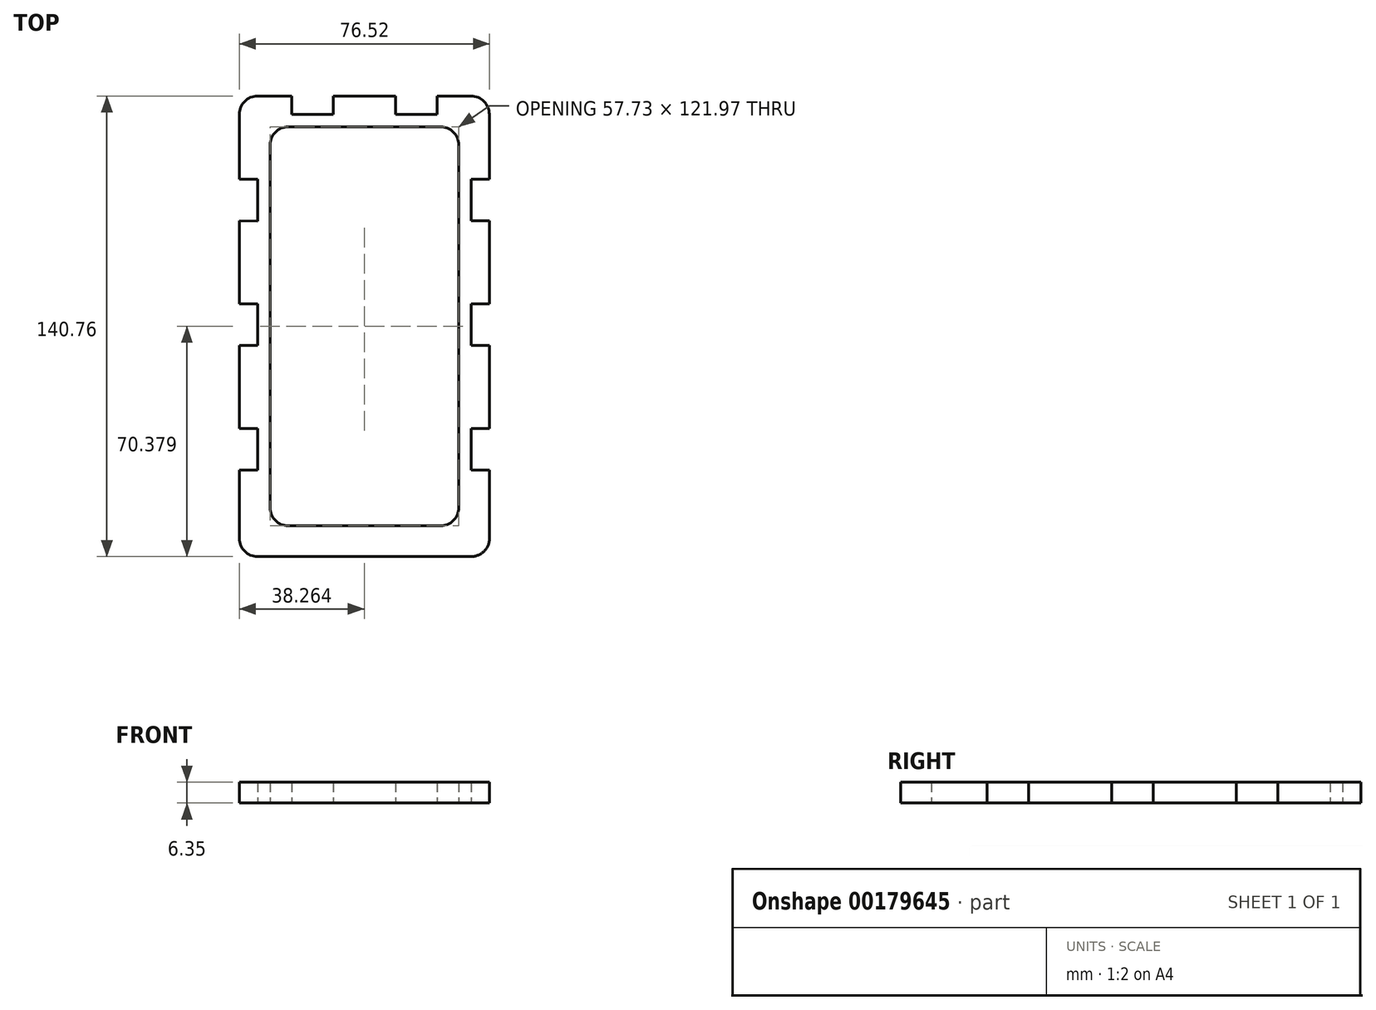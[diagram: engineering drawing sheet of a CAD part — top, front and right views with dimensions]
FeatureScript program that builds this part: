
annotation { "Feature Type Name" : "Feature", "Feature Type Description" : "" }
export const myFeature = defineFeature(function(context is Context, id is Id, definition is map)
    precondition{}
    {
        {
            var Q0;
            Q0=qCreatedBy(makeId("Top.planeOp"),FACE);
            var sketch = newSketch(context, id + "F0", { "sketchPlane" : qUnion([Q0])});
            skLineSegment(sketch, "E0.0", {"start": v(-32.64, 69.1) * mm, "end": v(-22.23, 69.1) * mm});
            skLineSegment(sketch, "E0.1", {"start": v(-38.23, 63.5) * mm, "end": v(-38.23, 43.7) * mm});
            skLineSegment(sketch, "E0.2", {"start": v(-32.64, -71.67) * mm, "end": v(-22.23, -71.67) * mm});
            skLineSegment(sketch, "E0.3", {"start": v(38.23, 63.5) * mm, "end": v(38.23, 43.7) * mm});
            skPoint(sketch, "E1", {"position": v(-38.23, 43.7) * mm});
            skPoint(sketch, "E2", {"position": v(38.23, 43.7) * mm});
            skPoint(sketch, "E3", {"position": v(-38.23, 31) * mm});
            skPoint(sketch, "E4", {"position": v(38.23, 31) * mm});
            skLineSegment(sketch, "E5", {"start": v(-38.23, 43.7) * mm, "end": v(-32.64, 43.7) * mm});
            skLineSegment(sketch, "E6", {"start": v(-38.23, 31) * mm, "end": v(-32.64, 30.78) * mm});
            skLineSegment(sketch, "E7", {"start": v(-32.64, 30.78) * mm, "end": v(-32.64, 43.7) * mm});
            skLineSegment(sketch, "E8.trimOffspring", {"start": v(-38.23, 31) * mm, "end": v(-38.23, 5.6) * mm});
            skLineSegment(sketch, "E9", {"start": v(38.23, 43.7) * mm, "end": v(32.64, 43.7) * mm});
            skLineSegment(sketch, "E10", {"start": v(38.23, 31) * mm, "end": v(32.64, 31) * mm});
            skLineSegment(sketch, "E11", {"start": v(32.64, 31) * mm, "end": v(32.64, 43.7) * mm});
            skLineSegment(sketch, "E12.trimOffspring", {"start": v(38.23, 31) * mm, "end": v(38.23, 5.6) * mm});
            skPoint(sketch, "E13", {"position": v(-38.23, 5.6) * mm});
            skPoint(sketch, "E14", {"position": v(38.23, 5.6) * mm});
            skPoint(sketch, "E15", {"position": v(-38.23, -7.1) * mm});
            skPoint(sketch, "E16", {"position": v(38.23, -7.1) * mm});
            skPoint(sketch, "E17", {"position": v(-38.23, -32.5) * mm});
            skPoint(sketch, "E18", {"position": v(38.23, -32.5) * mm});
            skPoint(sketch, "E19", {"position": v(38.23, -45.2) * mm});
            skLineSegment(sketch, "E20", {"start": v(-38.23, 5.6) * mm, "end": v(-32.64, 5.6) * mm});
            skLineSegment(sketch, "E21", {"start": v(-38.23, -7.1) * mm, "end": v(-32.64, -7.1) * mm});
            skLineSegment(sketch, "E22", {"start": v(-32.64, -7.1) * mm, "end": v(-32.64, 5.6) * mm});
            skLineSegment(sketch, "E23.trimOffspring", {"start": v(-38.23, -7.1) * mm, "end": v(-38.23, -32.5) * mm});
            skLineSegment(sketch, "E24.trimOffspring", {"start": v(-38.23, -52.57) * mm, "end": v(-38.23, -66.09) * mm});
            skLineSegment(sketch, "E25", {"start": v(-38.23, -32.5) * mm, "end": v(-32.64, -32.5) * mm});
            skLineSegment(sketch, "E26", {"start": v(-38.23, -45.2) * mm, "end": v(-32.64, -45.2) * mm});
            skLineSegment(sketch, "E27", {"start": v(-32.64, -45.2) * mm, "end": v(-32.64, -32.5) * mm});
            skLineSegment(sketch, "E28", {"start": v(38.23, 5.6) * mm, "end": v(32.64, 5.6) * mm});
            skLineSegment(sketch, "E29", {"start": v(38.23, -7.1) * mm, "end": v(32.64, -7.1) * mm});
            skLineSegment(sketch, "E30", {"start": v(32.64, -7.1) * mm, "end": v(32.64, 5.6) * mm});
            skLineSegment(sketch, "E31.trimOffspring", {"start": v(38.23, -7.1) * mm, "end": v(38.23, -32.5) * mm});
            skLineSegment(sketch, "E32", {"start": v(38.23, -32.5) * mm, "end": v(32.64, -32.5) * mm});
            skLineSegment(sketch, "E33", {"start": v(38.23, -45.2) * mm, "end": v(32.64, -45.2) * mm});
            skLineSegment(sketch, "E34", {"start": v(32.64, -45.2) * mm, "end": v(32.64, -32.5) * mm});
            skLineSegment(sketch, "E35.trimOffspring", {"start": v(38.23, -52.57) * mm, "end": v(38.3, -66.06) * mm});
            skLineSegment(sketch, "E36", {"start": v(-38.23, -45.2) * mm, "end": v(-38.23, -52.57) * mm});
            skLineSegment(sketch, "E37", {"start": v(38.23, -45.2) * mm, "end": v(38.23, -52.57) * mm});
            skPoint(sketch, "E38", {"position": v(-22.23, 69.1) * mm});
            skPoint(sketch, "E39", {"position": v(-9.53, 69.1) * mm});
            skPoint(sketch, "E40", {"position": v(9.52, 69.1) * mm});
            skPoint(sketch, "E41", {"position": v(22.22, 69.1) * mm});
            skLineSegment(sketch, "E42", {"start": v(-22.23, 69.1) * mm, "end": v(-22.23, 63.5) * mm});
            skLineSegment(sketch, "E43", {"start": v(-9.53, 69.1) * mm, "end": v(-9.53, 63.5) * mm});
            skLineSegment(sketch, "E44", {"start": v(-9.53, 63.5) * mm, "end": v(-22.23, 63.5) * mm});
            skLineSegment(sketch, "E45.trimOffspring", {"start": v(-9.53, 69.1) * mm, "end": v(9.52, 69.1) * mm});
            skLineSegment(sketch, "E46", {"start": v(9.52, 69.1) * mm, "end": v(9.52, 63.5) * mm});
            skLineSegment(sketch, "E47", {"start": v(22.22, 69.1) * mm, "end": v(22.22, 63.5) * mm});
            skLineSegment(sketch, "E48.trimOffspring", {"start": v(22.22, 69.1) * mm, "end": v(32.64, 69.1) * mm});
            skLineSegment(sketch, "E49", {"start": v(9.52, 63.5) * mm, "end": v(22.22, 63.5) * mm});
            skPoint(sketch, "E50", {"position": v(-22.23, -71.67) * mm});
            skPoint(sketch, "E51", {"position": v(-9.53, -71.67) * mm});
            skPoint(sketch, "E52", {"position": v(9.52, -71.67) * mm});
            skPoint(sketch, "E53", {"position": v(22.22, -71.67) * mm});
            skLineSegment(sketch, "E54.trimOffspring", {"start": v(-9.53, -71.67) * mm, "end": v(9.52, -71.67) * mm});
            skLineSegment(sketch, "E55.trimOffspring", {"start": v(22.22, -71.67) * mm, "end": v(32.7, -71.67) * mm});
            skPoint(sketch, "E56.visualSharp", {"position": v(-38.23, 69.1) * mm});
            skArc(sketch, "E56.filletArc", {"start": v(-32.64, 69.1) * mm, "mid": v(-36.6, 67.46) * mm, "end": v(-38.23, 63.5) * mm});
            skPoint(sketch, "E57.visualSharp", {"position": v(38.23, 69.1) * mm});
            skArc(sketch, "E57.filletArc", {"start": v(38.23, 63.5) * mm, "mid": v(36.6, 67.46) * mm, "end": v(32.64, 69.1) * mm});
            skPoint(sketch, "E58.visualSharp", {"position": v(38.32, -71.67) * mm});
            skArc(sketch, "E58.filletArc", {"start": v(32.7, -71.67) * mm, "mid": v(36.67, -70.03) * mm, "end": v(38.3, -66.06) * mm});
            skPoint(sketch, "E59.visualSharp", {"position": v(-38.23, -71.67) * mm});
            skArc(sketch, "E59.filletArc", {"start": v(-38.23, -66.09) * mm, "mid": v(-36.6, -70.04) * mm, "end": v(-32.64, -71.67) * mm});
            skLineSegment(sketch, "E60", {"start": v(-32.64, -71.67) * mm, "end": v(32.7, -71.67) * mm});
            skLineSegment(sketch, "E61.bottom", {"start": v(-32.64, 63.5) * mm, "end": v(32.7, 63.5) * mm, "construction": true});
            skLineSegment(sketch, "E61.top", {"start": v(-32.64, -66.09) * mm, "end": v(32.7, -66.09) * mm, "construction": true});
            skLineSegment(sketch, "E61.left", {"start": v(-32.64, 63.5) * mm, "end": v(-32.64, -66.09) * mm, "construction": true});
            skLineSegment(sketch, "E61.right", {"start": v(32.7, 63.5) * mm, "end": v(32.7, -66.09) * mm, "construction": true});
            skLineSegment(sketch, "E62.0", {"start": v(-28.83, 54.1) * mm, "end": v(-28.83, -56.69) * mm});
            skLineSegment(sketch, "E62.1", {"start": v(-23.24, 59.7) * mm, "end": v(23.3, 59.7) * mm});
            skLineSegment(sketch, "E62.2", {"start": v(28.9, 54.1) * mm, "end": v(28.9, -56.69) * mm});
            skLineSegment(sketch, "E62.3", {"start": v(-23.24, -62.28) * mm, "end": v(23.3, -62.28) * mm});
            skPoint(sketch, "E63.visualSharp", {"position": v(-28.83, 59.7) * mm});
            skArc(sketch, "E63.filletArc", {"start": v(-23.24, 59.7) * mm, "mid": v(-27.2, 58.06) * mm, "end": v(-28.83, 54.1) * mm});
            skPoint(sketch, "E64.visualSharp", {"position": v(28.9, 59.7) * mm});
            skArc(sketch, "E64.filletArc", {"start": v(28.9, 54.1) * mm, "mid": v(27.26, 58.06) * mm, "end": v(23.3, 59.7) * mm});
            skPoint(sketch, "E65.visualSharp", {"position": v(28.9, -62.28) * mm});
            skArc(sketch, "E65.filletArc", {"start": v(23.3, -62.28) * mm, "mid": v(27.26, -60.64) * mm, "end": v(28.9, -56.69) * mm});
            skPoint(sketch, "E66.visualSharp", {"position": v(-28.83, -62.28) * mm});
            skArc(sketch, "E66.filletArc", {"start": v(-28.83, -56.69) * mm, "mid": v(-27.2, -60.64) * mm, "end": v(-23.24, -62.28) * mm});
            skSolve(sketch);
        }
        {
            var Q0;
            Q0=makeQuery(id+"F0.imprint","IMPRINT",FACE,{"disambiguationData":[TD([[makeQuery(id+"F0.imprint","IMPRINT",EDGE,{"derivedFrom":sQuery(id+"F0.wireOp",EDGE,"E0.0")}),-1.0]])]});
            extrude(context, id + "F1", {"entities" : qUnion([Q0]), "depth" : 6.35 * mm});
        }
    });
